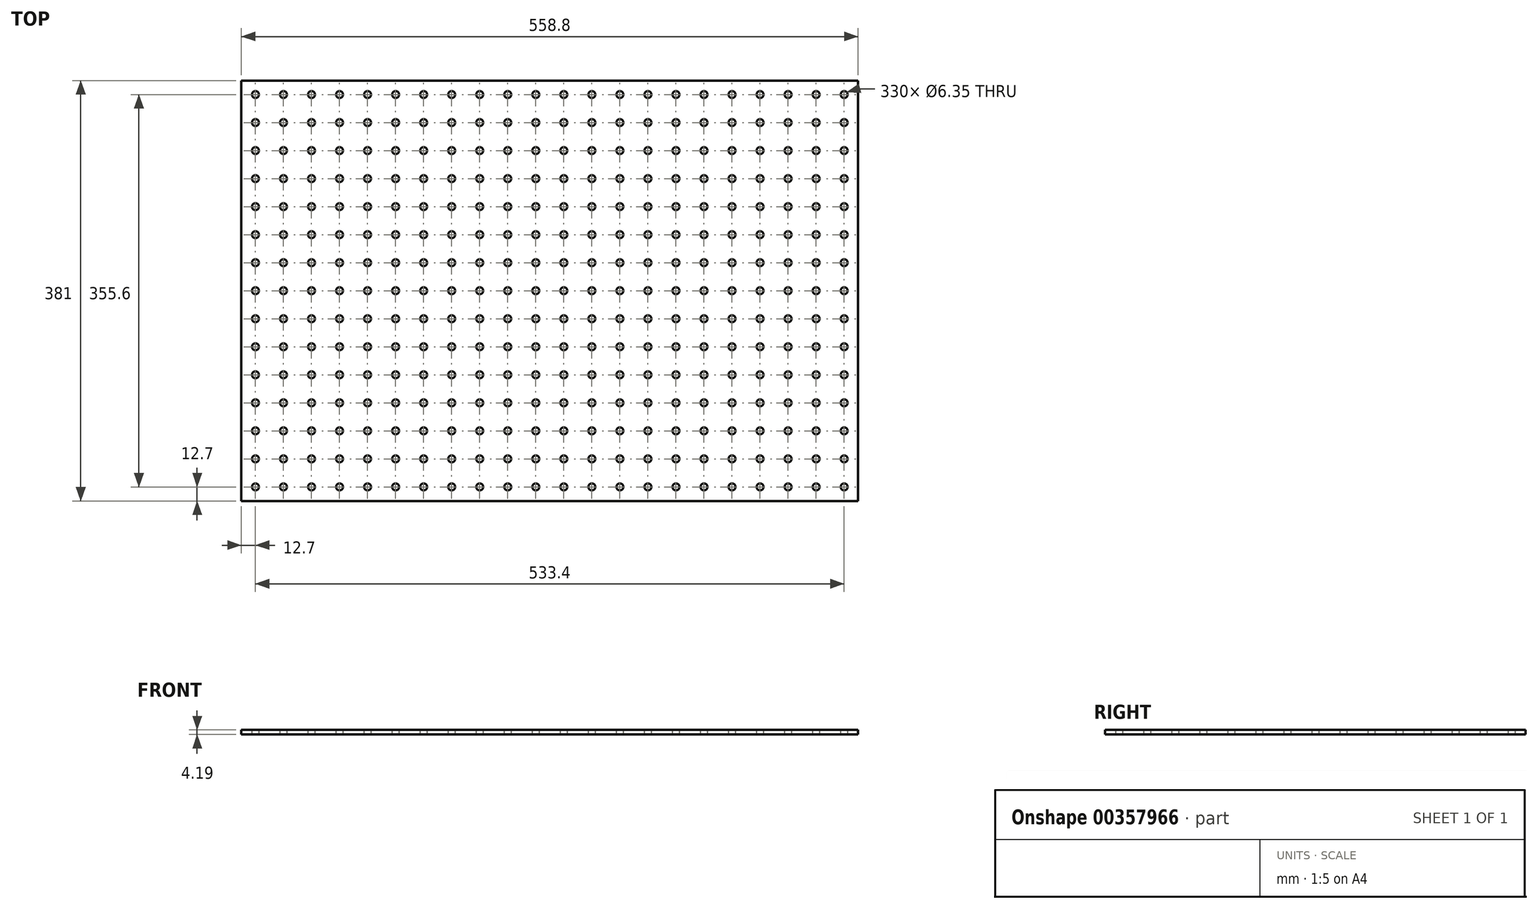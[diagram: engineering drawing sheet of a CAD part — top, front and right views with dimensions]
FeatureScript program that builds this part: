
annotation { "Feature Type Name" : "Feature", "Feature Type Description" : "" }
export const myFeature = defineFeature(function(context is Context, id is Id, definition is map)
    precondition{}
    {
        {
            var Q0;
            Q0=qCreatedBy(makeId("Top.planeOp"),FACE);
            var sketch = newSketch(context, id + "F0", { "sketchPlane" : qUnion([Q0])});
            skLineSegment(sketch, "E0.bottom", {"start": v(279.4, -190.5) * mm, "end": v(-279.4, -190.5) * mm});
            skLineSegment(sketch, "E0.top", {"start": v(279.4, 190.5) * mm, "end": v(-279.4, 190.5) * mm});
            skLineSegment(sketch, "E0.left", {"start": v(279.4, -190.5) * mm, "end": v(279.4, 190.5) * mm});
            skLineSegment(sketch, "E0.right", {"start": v(-279.4, -190.5) * mm, "end": v(-279.4, 190.5) * mm});
            skPoint(sketch, "E0.middle", {"position": v(0, 0) * mm});
            skCircle(sketch, "E1", {"center": v(266.7, 177.8) * mm, "radius": 3.17 * mm});
            skCircle(sketch, "E2.0.1.0", {"center": v(266.7, 152.4) * mm, "radius": 3.17 * mm});
            skCircle(sketch, "E2.0.2.0", {"center": v(266.7, 127) * mm, "radius": 3.17 * mm});
            skCircle(sketch, "E2.0.3.0", {"center": v(266.7, 101.6) * mm, "radius": 3.17 * mm});
            skCircle(sketch, "E2.0.4.0", {"center": v(266.7, 76.2) * mm, "radius": 3.17 * mm});
            skCircle(sketch, "E2.0.5.0", {"center": v(266.7, 50.8) * mm, "radius": 3.17 * mm});
            skCircle(sketch, "E2.0.6.0", {"center": v(266.7, 25.4) * mm, "radius": 3.17 * mm});
            skCircle(sketch, "E2.0.7.0", {"center": v(266.7, 0) * mm, "radius": 3.17 * mm});
            skCircle(sketch, "E2.0.8.0", {"center": v(266.7, -25.4) * mm, "radius": 3.17 * mm});
            skCircle(sketch, "E2.0.9.0", {"center": v(266.7, -50.8) * mm, "radius": 3.17 * mm});
            skCircle(sketch, "E2.0.10.0", {"center": v(266.7, -76.2) * mm, "radius": 3.17 * mm});
            skCircle(sketch, "E2.0.11.0", {"center": v(266.7, -101.6) * mm, "radius": 3.17 * mm});
            skCircle(sketch, "E2.0.12.0", {"center": v(266.7, -127) * mm, "radius": 3.17 * mm});
            skCircle(sketch, "E2.0.13.0", {"center": v(266.7, -152.4) * mm, "radius": 3.17 * mm});
            skCircle(sketch, "E2.0.14.0", {"center": v(266.7, -177.8) * mm, "radius": 3.17 * mm});
            skCircle(sketch, "E2.1.0.0", {"center": v(241.3, 177.8) * mm, "radius": 3.17 * mm});
            skCircle(sketch, "E2.1.1.0", {"center": v(241.3, 152.4) * mm, "radius": 3.17 * mm});
            skCircle(sketch, "E2.1.2.0", {"center": v(241.3, 127) * mm, "radius": 3.17 * mm});
            skCircle(sketch, "E2.1.3.0", {"center": v(241.3, 101.6) * mm, "radius": 3.17 * mm});
            skCircle(sketch, "E2.1.4.0", {"center": v(241.3, 76.2) * mm, "radius": 3.17 * mm});
            skCircle(sketch, "E2.1.5.0", {"center": v(241.3, 50.8) * mm, "radius": 3.17 * mm});
            skCircle(sketch, "E2.1.6.0", {"center": v(241.3, 25.4) * mm, "radius": 3.17 * mm});
            skCircle(sketch, "E2.1.7.0", {"center": v(241.3, 0) * mm, "radius": 3.17 * mm});
            skCircle(sketch, "E2.1.8.0", {"center": v(241.3, -25.4) * mm, "radius": 3.17 * mm});
            skCircle(sketch, "E2.1.9.0", {"center": v(241.3, -50.8) * mm, "radius": 3.17 * mm});
            skCircle(sketch, "E2.1.10.0", {"center": v(241.3, -76.2) * mm, "radius": 3.17 * mm});
            skCircle(sketch, "E2.1.11.0", {"center": v(241.3, -101.6) * mm, "radius": 3.17 * mm});
            skCircle(sketch, "E2.1.12.0", {"center": v(241.3, -127) * mm, "radius": 3.17 * mm});
            skCircle(sketch, "E2.1.13.0", {"center": v(241.3, -152.4) * mm, "radius": 3.17 * mm});
            skCircle(sketch, "E2.1.14.0", {"center": v(241.3, -177.8) * mm, "radius": 3.17 * mm});
            skCircle(sketch, "E2.2.0.0", {"center": v(215.9, 177.8) * mm, "radius": 3.17 * mm});
            skCircle(sketch, "E2.2.1.0", {"center": v(215.9, 152.4) * mm, "radius": 3.17 * mm});
            skCircle(sketch, "E2.2.2.0", {"center": v(215.9, 127) * mm, "radius": 3.17 * mm});
            skCircle(sketch, "E2.2.3.0", {"center": v(215.9, 101.6) * mm, "radius": 3.17 * mm});
            skCircle(sketch, "E2.2.4.0", {"center": v(215.9, 76.2) * mm, "radius": 3.17 * mm});
            skCircle(sketch, "E2.2.5.0", {"center": v(215.9, 50.8) * mm, "radius": 3.17 * mm});
            skCircle(sketch, "E2.2.6.0", {"center": v(215.9, 25.4) * mm, "radius": 3.17 * mm});
            skCircle(sketch, "E2.2.7.0", {"center": v(215.9, 0) * mm, "radius": 3.17 * mm});
            skCircle(sketch, "E2.2.8.0", {"center": v(215.9, -25.4) * mm, "radius": 3.17 * mm});
            skCircle(sketch, "E2.2.9.0", {"center": v(215.9, -50.8) * mm, "radius": 3.17 * mm});
            skCircle(sketch, "E2.2.10.0", {"center": v(215.9, -76.2) * mm, "radius": 3.17 * mm});
            skCircle(sketch, "E2.2.11.0", {"center": v(215.9, -101.6) * mm, "radius": 3.17 * mm});
            skCircle(sketch, "E2.2.12.0", {"center": v(215.9, -127) * mm, "radius": 3.17 * mm});
            skCircle(sketch, "E2.2.13.0", {"center": v(215.9, -152.4) * mm, "radius": 3.17 * mm});
            skCircle(sketch, "E2.2.14.0", {"center": v(215.9, -177.8) * mm, "radius": 3.17 * mm});
            skCircle(sketch, "E2.3.0.0", {"center": v(190.5, 177.8) * mm, "radius": 3.17 * mm});
            skCircle(sketch, "E2.3.1.0", {"center": v(190.5, 152.4) * mm, "radius": 3.17 * mm});
            skCircle(sketch, "E2.3.2.0", {"center": v(190.5, 127) * mm, "radius": 3.17 * mm});
            skCircle(sketch, "E2.3.3.0", {"center": v(190.5, 101.6) * mm, "radius": 3.17 * mm});
            skCircle(sketch, "E2.3.4.0", {"center": v(190.5, 76.2) * mm, "radius": 3.17 * mm});
            skCircle(sketch, "E2.3.5.0", {"center": v(190.5, 50.8) * mm, "radius": 3.17 * mm});
            skCircle(sketch, "E2.3.6.0", {"center": v(190.5, 25.4) * mm, "radius": 3.17 * mm});
            skCircle(sketch, "E2.3.7.0", {"center": v(190.5, 0) * mm, "radius": 3.17 * mm});
            skCircle(sketch, "E2.3.8.0", {"center": v(190.5, -25.4) * mm, "radius": 3.17 * mm});
            skCircle(sketch, "E2.3.9.0", {"center": v(190.5, -50.8) * mm, "radius": 3.17 * mm});
            skCircle(sketch, "E2.3.10.0", {"center": v(190.5, -76.2) * mm, "radius": 3.17 * mm});
            skCircle(sketch, "E2.3.11.0", {"center": v(190.5, -101.6) * mm, "radius": 3.17 * mm});
            skCircle(sketch, "E2.3.12.0", {"center": v(190.5, -127) * mm, "radius": 3.17 * mm});
            skCircle(sketch, "E2.3.13.0", {"center": v(190.5, -152.4) * mm, "radius": 3.17 * mm});
            skCircle(sketch, "E2.3.14.0", {"center": v(190.5, -177.8) * mm, "radius": 3.17 * mm});
            skCircle(sketch, "E2.4.0.0", {"center": v(165.1, 177.8) * mm, "radius": 3.17 * mm});
            skCircle(sketch, "E2.4.1.0", {"center": v(165.1, 152.4) * mm, "radius": 3.17 * mm});
            skCircle(sketch, "E2.4.2.0", {"center": v(165.1, 127) * mm, "radius": 3.17 * mm});
            skCircle(sketch, "E2.4.3.0", {"center": v(165.1, 101.6) * mm, "radius": 3.17 * mm});
            skCircle(sketch, "E2.4.4.0", {"center": v(165.1, 76.2) * mm, "radius": 3.17 * mm});
            skCircle(sketch, "E2.4.5.0", {"center": v(165.1, 50.8) * mm, "radius": 3.17 * mm});
            skCircle(sketch, "E2.4.6.0", {"center": v(165.1, 25.4) * mm, "radius": 3.17 * mm});
            skCircle(sketch, "E2.4.7.0", {"center": v(165.1, 0) * mm, "radius": 3.17 * mm});
            skCircle(sketch, "E2.4.8.0", {"center": v(165.1, -25.4) * mm, "radius": 3.17 * mm});
            skCircle(sketch, "E2.4.9.0", {"center": v(165.1, -50.8) * mm, "radius": 3.17 * mm});
            skCircle(sketch, "E2.4.10.0", {"center": v(165.1, -76.2) * mm, "radius": 3.17 * mm});
            skCircle(sketch, "E2.4.11.0", {"center": v(165.1, -101.6) * mm, "radius": 3.17 * mm});
            skCircle(sketch, "E2.4.12.0", {"center": v(165.1, -127) * mm, "radius": 3.17 * mm});
            skCircle(sketch, "E2.4.13.0", {"center": v(165.1, -152.4) * mm, "radius": 3.17 * mm});
            skCircle(sketch, "E2.4.14.0", {"center": v(165.1, -177.8) * mm, "radius": 3.17 * mm});
            skCircle(sketch, "E2.5.0.0", {"center": v(139.7, 177.8) * mm, "radius": 3.17 * mm});
            skCircle(sketch, "E2.5.1.0", {"center": v(139.7, 152.4) * mm, "radius": 3.17 * mm});
            skCircle(sketch, "E2.5.2.0", {"center": v(139.7, 127) * mm, "radius": 3.17 * mm});
            skCircle(sketch, "E2.5.3.0", {"center": v(139.7, 101.6) * mm, "radius": 3.17 * mm});
            skCircle(sketch, "E2.5.4.0", {"center": v(139.7, 76.2) * mm, "radius": 3.17 * mm});
            skCircle(sketch, "E2.5.5.0", {"center": v(139.7, 50.8) * mm, "radius": 3.17 * mm});
            skCircle(sketch, "E2.5.6.0", {"center": v(139.7, 25.4) * mm, "radius": 3.17 * mm});
            skCircle(sketch, "E2.5.7.0", {"center": v(139.7, 0) * mm, "radius": 3.17 * mm});
            skCircle(sketch, "E2.5.8.0", {"center": v(139.7, -25.4) * mm, "radius": 3.17 * mm});
            skCircle(sketch, "E2.5.9.0", {"center": v(139.7, -50.8) * mm, "radius": 3.17 * mm});
            skCircle(sketch, "E2.5.10.0", {"center": v(139.7, -76.2) * mm, "radius": 3.17 * mm});
            skCircle(sketch, "E2.5.11.0", {"center": v(139.7, -101.6) * mm, "radius": 3.17 * mm});
            skCircle(sketch, "E2.5.12.0", {"center": v(139.7, -127) * mm, "radius": 3.17 * mm});
            skCircle(sketch, "E2.5.13.0", {"center": v(139.7, -152.4) * mm, "radius": 3.17 * mm});
            skCircle(sketch, "E2.5.14.0", {"center": v(139.7, -177.8) * mm, "radius": 3.17 * mm});
            skCircle(sketch, "E2.6.0.0", {"center": v(114.3, 177.8) * mm, "radius": 3.17 * mm});
            skCircle(sketch, "E2.6.1.0", {"center": v(114.3, 152.4) * mm, "radius": 3.17 * mm});
            skCircle(sketch, "E2.6.2.0", {"center": v(114.3, 127) * mm, "radius": 3.17 * mm});
            skCircle(sketch, "E2.6.3.0", {"center": v(114.3, 101.6) * mm, "radius": 3.17 * mm});
            skCircle(sketch, "E2.6.4.0", {"center": v(114.3, 76.2) * mm, "radius": 3.17 * mm});
            skCircle(sketch, "E2.6.5.0", {"center": v(114.3, 50.8) * mm, "radius": 3.17 * mm});
            skCircle(sketch, "E2.6.6.0", {"center": v(114.3, 25.4) * mm, "radius": 3.17 * mm});
            skCircle(sketch, "E2.6.7.0", {"center": v(114.3, 0) * mm, "radius": 3.17 * mm});
            skCircle(sketch, "E2.6.8.0", {"center": v(114.3, -25.4) * mm, "radius": 3.17 * mm});
            skCircle(sketch, "E2.6.9.0", {"center": v(114.3, -50.8) * mm, "radius": 3.17 * mm});
            skCircle(sketch, "E2.6.10.0", {"center": v(114.3, -76.2) * mm, "radius": 3.17 * mm});
            skCircle(sketch, "E2.6.11.0", {"center": v(114.3, -101.6) * mm, "radius": 3.17 * mm});
            skCircle(sketch, "E2.6.12.0", {"center": v(114.3, -127) * mm, "radius": 3.17 * mm});
            skCircle(sketch, "E2.6.13.0", {"center": v(114.3, -152.4) * mm, "radius": 3.17 * mm});
            skCircle(sketch, "E2.6.14.0", {"center": v(114.3, -177.8) * mm, "radius": 3.17 * mm});
            skCircle(sketch, "E2.7.0.0", {"center": v(88.9, 177.8) * mm, "radius": 3.17 * mm});
            skCircle(sketch, "E2.7.1.0", {"center": v(88.9, 152.4) * mm, "radius": 3.17 * mm});
            skCircle(sketch, "E2.7.2.0", {"center": v(88.9, 127) * mm, "radius": 3.17 * mm});
            skCircle(sketch, "E2.7.3.0", {"center": v(88.9, 101.6) * mm, "radius": 3.17 * mm});
            skCircle(sketch, "E2.7.4.0", {"center": v(88.9, 76.2) * mm, "radius": 3.17 * mm});
            skCircle(sketch, "E2.7.5.0", {"center": v(88.9, 50.8) * mm, "radius": 3.17 * mm});
            skCircle(sketch, "E2.7.6.0", {"center": v(88.9, 25.4) * mm, "radius": 3.17 * mm});
            skCircle(sketch, "E2.7.7.0", {"center": v(88.9, 0) * mm, "radius": 3.17 * mm});
            skCircle(sketch, "E2.7.8.0", {"center": v(88.9, -25.4) * mm, "radius": 3.17 * mm});
            skCircle(sketch, "E2.7.9.0", {"center": v(88.9, -50.8) * mm, "radius": 3.17 * mm});
            skCircle(sketch, "E2.7.10.0", {"center": v(88.9, -76.2) * mm, "radius": 3.17 * mm});
            skCircle(sketch, "E2.7.11.0", {"center": v(88.9, -101.6) * mm, "radius": 3.17 * mm});
            skCircle(sketch, "E2.7.12.0", {"center": v(88.9, -127) * mm, "radius": 3.17 * mm});
            skCircle(sketch, "E2.7.13.0", {"center": v(88.9, -152.4) * mm, "radius": 3.17 * mm});
            skCircle(sketch, "E2.7.14.0", {"center": v(88.9, -177.8) * mm, "radius": 3.17 * mm});
            skCircle(sketch, "E2.8.0.0", {"center": v(63.5, 177.8) * mm, "radius": 3.17 * mm});
            skCircle(sketch, "E2.8.1.0", {"center": v(63.5, 152.4) * mm, "radius": 3.17 * mm});
            skCircle(sketch, "E2.8.2.0", {"center": v(63.5, 127) * mm, "radius": 3.17 * mm});
            skCircle(sketch, "E2.8.3.0", {"center": v(63.5, 101.6) * mm, "radius": 3.17 * mm});
            skCircle(sketch, "E2.8.4.0", {"center": v(63.5, 76.2) * mm, "radius": 3.17 * mm});
            skCircle(sketch, "E2.8.5.0", {"center": v(63.5, 50.8) * mm, "radius": 3.17 * mm});
            skCircle(sketch, "E2.8.6.0", {"center": v(63.5, 25.4) * mm, "radius": 3.17 * mm});
            skCircle(sketch, "E2.8.7.0", {"center": v(63.5, 0) * mm, "radius": 3.17 * mm});
            skCircle(sketch, "E2.8.8.0", {"center": v(63.5, -25.4) * mm, "radius": 3.17 * mm});
            skCircle(sketch, "E2.8.9.0", {"center": v(63.5, -50.8) * mm, "radius": 3.17 * mm});
            skCircle(sketch, "E2.8.10.0", {"center": v(63.5, -76.2) * mm, "radius": 3.17 * mm});
            skCircle(sketch, "E2.8.11.0", {"center": v(63.5, -101.6) * mm, "radius": 3.17 * mm});
            skCircle(sketch, "E2.8.12.0", {"center": v(63.5, -127) * mm, "radius": 3.17 * mm});
            skCircle(sketch, "E2.8.13.0", {"center": v(63.5, -152.4) * mm, "radius": 3.17 * mm});
            skCircle(sketch, "E2.8.14.0", {"center": v(63.5, -177.8) * mm, "radius": 3.17 * mm});
            skCircle(sketch, "E2.9.0.0", {"center": v(38.1, 177.8) * mm, "radius": 3.17 * mm});
            skCircle(sketch, "E2.9.1.0", {"center": v(38.1, 152.4) * mm, "radius": 3.17 * mm});
            skCircle(sketch, "E2.9.2.0", {"center": v(38.1, 127) * mm, "radius": 3.17 * mm});
            skCircle(sketch, "E2.9.3.0", {"center": v(38.1, 101.6) * mm, "radius": 3.17 * mm});
            skCircle(sketch, "E2.9.4.0", {"center": v(38.1, 76.2) * mm, "radius": 3.17 * mm});
            skCircle(sketch, "E2.9.5.0", {"center": v(38.1, 50.8) * mm, "radius": 3.17 * mm});
            skCircle(sketch, "E2.9.6.0", {"center": v(38.1, 25.4) * mm, "radius": 3.17 * mm});
            skCircle(sketch, "E2.9.7.0", {"center": v(38.1, 0) * mm, "radius": 3.17 * mm});
            skCircle(sketch, "E2.9.8.0", {"center": v(38.1, -25.4) * mm, "radius": 3.17 * mm});
            skCircle(sketch, "E2.9.9.0", {"center": v(38.1, -50.8) * mm, "radius": 3.17 * mm});
            skCircle(sketch, "E2.9.10.0", {"center": v(38.1, -76.2) * mm, "radius": 3.17 * mm});
            skCircle(sketch, "E2.9.11.0", {"center": v(38.1, -101.6) * mm, "radius": 3.17 * mm});
            skCircle(sketch, "E2.9.12.0", {"center": v(38.1, -127) * mm, "radius": 3.17 * mm});
            skCircle(sketch, "E2.9.13.0", {"center": v(38.1, -152.4) * mm, "radius": 3.17 * mm});
            skCircle(sketch, "E2.9.14.0", {"center": v(38.1, -177.8) * mm, "radius": 3.17 * mm});
            skCircle(sketch, "E2.10.0.0", {"center": v(12.7, 177.8) * mm, "radius": 3.17 * mm});
            skCircle(sketch, "E2.10.1.0", {"center": v(12.7, 152.4) * mm, "radius": 3.17 * mm});
            skCircle(sketch, "E2.10.2.0", {"center": v(12.7, 127) * mm, "radius": 3.17 * mm});
            skCircle(sketch, "E2.10.3.0", {"center": v(12.7, 101.6) * mm, "radius": 3.17 * mm});
            skCircle(sketch, "E2.10.4.0", {"center": v(12.7, 76.2) * mm, "radius": 3.17 * mm});
            skCircle(sketch, "E2.10.5.0", {"center": v(12.7, 50.8) * mm, "radius": 3.17 * mm});
            skCircle(sketch, "E2.10.6.0", {"center": v(12.7, 25.4) * mm, "radius": 3.17 * mm});
            skCircle(sketch, "E2.10.7.0", {"center": v(12.7, 0) * mm, "radius": 3.17 * mm});
            skCircle(sketch, "E2.10.8.0", {"center": v(12.7, -25.4) * mm, "radius": 3.17 * mm});
            skCircle(sketch, "E2.10.9.0", {"center": v(12.7, -50.8) * mm, "radius": 3.17 * mm});
            skCircle(sketch, "E2.10.10.0", {"center": v(12.7, -76.2) * mm, "radius": 3.17 * mm});
            skCircle(sketch, "E2.10.11.0", {"center": v(12.7, -101.6) * mm, "radius": 3.17 * mm});
            skCircle(sketch, "E2.10.12.0", {"center": v(12.7, -127) * mm, "radius": 3.17 * mm});
            skCircle(sketch, "E2.10.13.0", {"center": v(12.7, -152.4) * mm, "radius": 3.17 * mm});
            skCircle(sketch, "E2.10.14.0", {"center": v(12.7, -177.8) * mm, "radius": 3.17 * mm});
            skCircle(sketch, "E2.11.0.0", {"center": v(-12.7, 177.8) * mm, "radius": 3.17 * mm});
            skCircle(sketch, "E2.11.1.0", {"center": v(-12.7, 152.4) * mm, "radius": 3.17 * mm});
            skCircle(sketch, "E2.11.2.0", {"center": v(-12.7, 127) * mm, "radius": 3.17 * mm});
            skCircle(sketch, "E2.11.3.0", {"center": v(-12.7, 101.6) * mm, "radius": 3.17 * mm});
            skCircle(sketch, "E2.11.4.0", {"center": v(-12.7, 76.2) * mm, "radius": 3.17 * mm});
            skCircle(sketch, "E2.11.5.0", {"center": v(-12.7, 50.8) * mm, "radius": 3.17 * mm});
            skCircle(sketch, "E2.11.6.0", {"center": v(-12.7, 25.4) * mm, "radius": 3.17 * mm});
            skCircle(sketch, "E2.11.7.0", {"center": v(-12.7, 0) * mm, "radius": 3.17 * mm});
            skCircle(sketch, "E2.11.8.0", {"center": v(-12.7, -25.4) * mm, "radius": 3.17 * mm});
            skCircle(sketch, "E2.11.9.0", {"center": v(-12.7, -50.8) * mm, "radius": 3.17 * mm});
            skCircle(sketch, "E2.11.10.0", {"center": v(-12.7, -76.2) * mm, "radius": 3.17 * mm});
            skCircle(sketch, "E2.11.11.0", {"center": v(-12.7, -101.6) * mm, "radius": 3.17 * mm});
            skCircle(sketch, "E2.11.12.0", {"center": v(-12.7, -127) * mm, "radius": 3.17 * mm});
            skCircle(sketch, "E2.11.13.0", {"center": v(-12.7, -152.4) * mm, "radius": 3.17 * mm});
            skCircle(sketch, "E2.11.14.0", {"center": v(-12.7, -177.8) * mm, "radius": 3.17 * mm});
            skCircle(sketch, "E2.12.0.0", {"center": v(-38.1, 177.8) * mm, "radius": 3.17 * mm});
            skCircle(sketch, "E2.12.1.0", {"center": v(-38.1, 152.4) * mm, "radius": 3.17 * mm});
            skCircle(sketch, "E2.12.2.0", {"center": v(-38.1, 127) * mm, "radius": 3.17 * mm});
            skCircle(sketch, "E2.12.3.0", {"center": v(-38.1, 101.6) * mm, "radius": 3.17 * mm});
            skCircle(sketch, "E2.12.4.0", {"center": v(-38.1, 76.2) * mm, "radius": 3.17 * mm});
            skCircle(sketch, "E2.12.5.0", {"center": v(-38.1, 50.8) * mm, "radius": 3.17 * mm});
            skCircle(sketch, "E2.12.6.0", {"center": v(-38.1, 25.4) * mm, "radius": 3.17 * mm});
            skCircle(sketch, "E2.12.7.0", {"center": v(-38.1, 0) * mm, "radius": 3.17 * mm});
            skCircle(sketch, "E2.12.8.0", {"center": v(-38.1, -25.4) * mm, "radius": 3.17 * mm});
            skCircle(sketch, "E2.12.9.0", {"center": v(-38.1, -50.8) * mm, "radius": 3.17 * mm});
            skCircle(sketch, "E2.12.10.0", {"center": v(-38.1, -76.2) * mm, "radius": 3.17 * mm});
            skCircle(sketch, "E2.12.11.0", {"center": v(-38.1, -101.6) * mm, "radius": 3.17 * mm});
            skCircle(sketch, "E2.12.12.0", {"center": v(-38.1, -127) * mm, "radius": 3.17 * mm});
            skCircle(sketch, "E2.12.13.0", {"center": v(-38.1, -152.4) * mm, "radius": 3.17 * mm});
            skCircle(sketch, "E2.12.14.0", {"center": v(-38.1, -177.8) * mm, "radius": 3.17 * mm});
            skCircle(sketch, "E2.13.0.0", {"center": v(-63.5, 177.8) * mm, "radius": 3.17 * mm});
            skCircle(sketch, "E2.13.1.0", {"center": v(-63.5, 152.4) * mm, "radius": 3.17 * mm});
            skCircle(sketch, "E2.13.2.0", {"center": v(-63.5, 127) * mm, "radius": 3.17 * mm});
            skCircle(sketch, "E2.13.3.0", {"center": v(-63.5, 101.6) * mm, "radius": 3.17 * mm});
            skCircle(sketch, "E2.13.4.0", {"center": v(-63.5, 76.2) * mm, "radius": 3.17 * mm});
            skCircle(sketch, "E2.13.5.0", {"center": v(-63.5, 50.8) * mm, "radius": 3.17 * mm});
            skCircle(sketch, "E2.13.6.0", {"center": v(-63.5, 25.4) * mm, "radius": 3.17 * mm});
            skCircle(sketch, "E2.13.7.0", {"center": v(-63.5, 0) * mm, "radius": 3.17 * mm});
            skCircle(sketch, "E2.13.8.0", {"center": v(-63.5, -25.4) * mm, "radius": 3.17 * mm});
            skCircle(sketch, "E2.13.9.0", {"center": v(-63.5, -50.8) * mm, "radius": 3.17 * mm});
            skCircle(sketch, "E2.13.10.0", {"center": v(-63.5, -76.2) * mm, "radius": 3.17 * mm});
            skCircle(sketch, "E2.13.11.0", {"center": v(-63.5, -101.6) * mm, "radius": 3.17 * mm});
            skCircle(sketch, "E2.13.12.0", {"center": v(-63.5, -127) * mm, "radius": 3.17 * mm});
            skCircle(sketch, "E2.13.13.0", {"center": v(-63.5, -152.4) * mm, "radius": 3.17 * mm});
            skCircle(sketch, "E2.13.14.0", {"center": v(-63.5, -177.8) * mm, "radius": 3.17 * mm});
            skCircle(sketch, "E2.14.0.0", {"center": v(-88.9, 177.8) * mm, "radius": 3.17 * mm});
            skCircle(sketch, "E2.14.1.0", {"center": v(-88.9, 152.4) * mm, "radius": 3.17 * mm});
            skCircle(sketch, "E2.14.2.0", {"center": v(-88.9, 127) * mm, "radius": 3.17 * mm});
            skCircle(sketch, "E2.14.3.0", {"center": v(-88.9, 101.6) * mm, "radius": 3.17 * mm});
            skCircle(sketch, "E2.14.4.0", {"center": v(-88.9, 76.2) * mm, "radius": 3.17 * mm});
            skCircle(sketch, "E2.14.5.0", {"center": v(-88.9, 50.8) * mm, "radius": 3.17 * mm});
            skCircle(sketch, "E2.14.6.0", {"center": v(-88.9, 25.4) * mm, "radius": 3.17 * mm});
            skCircle(sketch, "E2.14.7.0", {"center": v(-88.9, 0) * mm, "radius": 3.17 * mm});
            skCircle(sketch, "E2.14.8.0", {"center": v(-88.9, -25.4) * mm, "radius": 3.17 * mm});
            skCircle(sketch, "E2.14.9.0", {"center": v(-88.9, -50.8) * mm, "radius": 3.17 * mm});
            skCircle(sketch, "E2.14.10.0", {"center": v(-88.9, -76.2) * mm, "radius": 3.17 * mm});
            skCircle(sketch, "E2.14.11.0", {"center": v(-88.9, -101.6) * mm, "radius": 3.17 * mm});
            skCircle(sketch, "E2.14.12.0", {"center": v(-88.9, -127) * mm, "radius": 3.17 * mm});
            skCircle(sketch, "E2.14.13.0", {"center": v(-88.9, -152.4) * mm, "radius": 3.17 * mm});
            skCircle(sketch, "E2.14.14.0", {"center": v(-88.9, -177.8) * mm, "radius": 3.17 * mm});
            skCircle(sketch, "E2.15.0.0", {"center": v(-114.3, 177.8) * mm, "radius": 3.17 * mm});
            skCircle(sketch, "E2.15.1.0", {"center": v(-114.3, 152.4) * mm, "radius": 3.17 * mm});
            skCircle(sketch, "E2.15.2.0", {"center": v(-114.3, 127) * mm, "radius": 3.17 * mm});
            skCircle(sketch, "E2.15.3.0", {"center": v(-114.3, 101.6) * mm, "radius": 3.17 * mm});
            skCircle(sketch, "E2.15.4.0", {"center": v(-114.3, 76.2) * mm, "radius": 3.17 * mm});
            skCircle(sketch, "E2.15.5.0", {"center": v(-114.3, 50.8) * mm, "radius": 3.17 * mm});
            skCircle(sketch, "E2.15.6.0", {"center": v(-114.3, 25.4) * mm, "radius": 3.17 * mm});
            skCircle(sketch, "E2.15.7.0", {"center": v(-114.3, 0) * mm, "radius": 3.17 * mm});
            skCircle(sketch, "E2.15.8.0", {"center": v(-114.3, -25.4) * mm, "radius": 3.17 * mm});
            skCircle(sketch, "E2.15.9.0", {"center": v(-114.3, -50.8) * mm, "radius": 3.17 * mm});
            skCircle(sketch, "E2.15.10.0", {"center": v(-114.3, -76.2) * mm, "radius": 3.17 * mm});
            skCircle(sketch, "E2.15.11.0", {"center": v(-114.3, -101.6) * mm, "radius": 3.17 * mm});
            skCircle(sketch, "E2.15.12.0", {"center": v(-114.3, -127) * mm, "radius": 3.17 * mm});
            skCircle(sketch, "E2.15.13.0", {"center": v(-114.3, -152.4) * mm, "radius": 3.17 * mm});
            skCircle(sketch, "E2.15.14.0", {"center": v(-114.3, -177.8) * mm, "radius": 3.17 * mm});
            skCircle(sketch, "E2.16.0.0", {"center": v(-139.7, 177.8) * mm, "radius": 3.17 * mm});
            skCircle(sketch, "E2.16.1.0", {"center": v(-139.7, 152.4) * mm, "radius": 3.17 * mm});
            skCircle(sketch, "E2.16.2.0", {"center": v(-139.7, 127) * mm, "radius": 3.17 * mm});
            skCircle(sketch, "E2.16.3.0", {"center": v(-139.7, 101.6) * mm, "radius": 3.17 * mm});
            skCircle(sketch, "E2.16.4.0", {"center": v(-139.7, 76.2) * mm, "radius": 3.17 * mm});
            skCircle(sketch, "E2.16.5.0", {"center": v(-139.7, 50.8) * mm, "radius": 3.17 * mm});
            skCircle(sketch, "E2.16.6.0", {"center": v(-139.7, 25.4) * mm, "radius": 3.17 * mm});
            skCircle(sketch, "E2.16.7.0", {"center": v(-139.7, 0) * mm, "radius": 3.17 * mm});
            skCircle(sketch, "E2.16.8.0", {"center": v(-139.7, -25.4) * mm, "radius": 3.17 * mm});
            skCircle(sketch, "E2.16.9.0", {"center": v(-139.7, -50.8) * mm, "radius": 3.17 * mm});
            skCircle(sketch, "E2.16.10.0", {"center": v(-139.7, -76.2) * mm, "radius": 3.17 * mm});
            skCircle(sketch, "E2.16.11.0", {"center": v(-139.7, -101.6) * mm, "radius": 3.17 * mm});
            skCircle(sketch, "E2.16.12.0", {"center": v(-139.7, -127) * mm, "radius": 3.17 * mm});
            skCircle(sketch, "E2.16.13.0", {"center": v(-139.7, -152.4) * mm, "radius": 3.17 * mm});
            skCircle(sketch, "E2.16.14.0", {"center": v(-139.7, -177.8) * mm, "radius": 3.17 * mm});
            skCircle(sketch, "E2.17.0.0", {"center": v(-165.1, 177.8) * mm, "radius": 3.17 * mm});
            skCircle(sketch, "E2.17.1.0", {"center": v(-165.1, 152.4) * mm, "radius": 3.17 * mm});
            skCircle(sketch, "E2.17.2.0", {"center": v(-165.1, 127) * mm, "radius": 3.17 * mm});
            skCircle(sketch, "E2.17.3.0", {"center": v(-165.1, 101.6) * mm, "radius": 3.17 * mm});
            skCircle(sketch, "E2.17.4.0", {"center": v(-165.1, 76.2) * mm, "radius": 3.17 * mm});
            skCircle(sketch, "E2.17.5.0", {"center": v(-165.1, 50.8) * mm, "radius": 3.17 * mm});
            skCircle(sketch, "E2.17.6.0", {"center": v(-165.1, 25.4) * mm, "radius": 3.17 * mm});
            skCircle(sketch, "E2.17.7.0", {"center": v(-165.1, 0) * mm, "radius": 3.17 * mm});
            skCircle(sketch, "E2.17.8.0", {"center": v(-165.1, -25.4) * mm, "radius": 3.17 * mm});
            skCircle(sketch, "E2.17.9.0", {"center": v(-165.1, -50.8) * mm, "radius": 3.17 * mm});
            skCircle(sketch, "E2.17.10.0", {"center": v(-165.1, -76.2) * mm, "radius": 3.17 * mm});
            skCircle(sketch, "E2.17.11.0", {"center": v(-165.1, -101.6) * mm, "radius": 3.17 * mm});
            skCircle(sketch, "E2.17.12.0", {"center": v(-165.1, -127) * mm, "radius": 3.17 * mm});
            skCircle(sketch, "E2.17.13.0", {"center": v(-165.1, -152.4) * mm, "radius": 3.17 * mm});
            skCircle(sketch, "E2.17.14.0", {"center": v(-165.1, -177.8) * mm, "radius": 3.17 * mm});
            skCircle(sketch, "E2.18.0.0", {"center": v(-190.5, 177.8) * mm, "radius": 3.17 * mm});
            skCircle(sketch, "E2.18.1.0", {"center": v(-190.5, 152.4) * mm, "radius": 3.17 * mm});
            skCircle(sketch, "E2.18.2.0", {"center": v(-190.5, 127) * mm, "radius": 3.17 * mm});
            skCircle(sketch, "E2.18.3.0", {"center": v(-190.5, 101.6) * mm, "radius": 3.17 * mm});
            skCircle(sketch, "E2.18.4.0", {"center": v(-190.5, 76.2) * mm, "radius": 3.17 * mm});
            skCircle(sketch, "E2.18.5.0", {"center": v(-190.5, 50.8) * mm, "radius": 3.17 * mm});
            skCircle(sketch, "E2.18.6.0", {"center": v(-190.5, 25.4) * mm, "radius": 3.17 * mm});
            skCircle(sketch, "E2.18.7.0", {"center": v(-190.5, 0) * mm, "radius": 3.17 * mm});
            skCircle(sketch, "E2.18.8.0", {"center": v(-190.5, -25.4) * mm, "radius": 3.17 * mm});
            skCircle(sketch, "E2.18.9.0", {"center": v(-190.5, -50.8) * mm, "radius": 3.17 * mm});
            skCircle(sketch, "E2.18.10.0", {"center": v(-190.5, -76.2) * mm, "radius": 3.17 * mm});
            skCircle(sketch, "E2.18.11.0", {"center": v(-190.5, -101.6) * mm, "radius": 3.17 * mm});
            skCircle(sketch, "E2.18.12.0", {"center": v(-190.5, -127) * mm, "radius": 3.17 * mm});
            skCircle(sketch, "E2.18.13.0", {"center": v(-190.5, -152.4) * mm, "radius": 3.17 * mm});
            skCircle(sketch, "E2.18.14.0", {"center": v(-190.5, -177.8) * mm, "radius": 3.17 * mm});
            skCircle(sketch, "E2.19.0.0", {"center": v(-215.9, 177.8) * mm, "radius": 3.17 * mm});
            skCircle(sketch, "E2.19.1.0", {"center": v(-215.9, 152.4) * mm, "radius": 3.17 * mm});
            skCircle(sketch, "E2.19.2.0", {"center": v(-215.9, 127) * mm, "radius": 3.17 * mm});
            skCircle(sketch, "E2.19.3.0", {"center": v(-215.9, 101.6) * mm, "radius": 3.17 * mm});
            skCircle(sketch, "E2.19.4.0", {"center": v(-215.9, 76.2) * mm, "radius": 3.17 * mm});
            skCircle(sketch, "E2.19.5.0", {"center": v(-215.9, 50.8) * mm, "radius": 3.17 * mm});
            skCircle(sketch, "E2.19.6.0", {"center": v(-215.9, 25.4) * mm, "radius": 3.17 * mm});
            skCircle(sketch, "E2.19.7.0", {"center": v(-215.9, 0) * mm, "radius": 3.17 * mm});
            skCircle(sketch, "E2.19.8.0", {"center": v(-215.9, -25.4) * mm, "radius": 3.17 * mm});
            skCircle(sketch, "E2.19.9.0", {"center": v(-215.9, -50.8) * mm, "radius": 3.17 * mm});
            skCircle(sketch, "E2.19.10.0", {"center": v(-215.9, -76.2) * mm, "radius": 3.17 * mm});
            skCircle(sketch, "E2.19.11.0", {"center": v(-215.9, -101.6) * mm, "radius": 3.17 * mm});
            skCircle(sketch, "E2.19.12.0", {"center": v(-215.9, -127) * mm, "radius": 3.17 * mm});
            skCircle(sketch, "E2.19.13.0", {"center": v(-215.9, -152.4) * mm, "radius": 3.17 * mm});
            skCircle(sketch, "E2.19.14.0", {"center": v(-215.9, -177.8) * mm, "radius": 3.17 * mm});
            skCircle(sketch, "E2.20.0.0", {"center": v(-241.3, 177.8) * mm, "radius": 3.17 * mm});
            skCircle(sketch, "E2.20.1.0", {"center": v(-241.3, 152.4) * mm, "radius": 3.17 * mm});
            skCircle(sketch, "E2.20.2.0", {"center": v(-241.3, 127) * mm, "radius": 3.17 * mm});
            skCircle(sketch, "E2.20.3.0", {"center": v(-241.3, 101.6) * mm, "radius": 3.17 * mm});
            skCircle(sketch, "E2.20.4.0", {"center": v(-241.3, 76.2) * mm, "radius": 3.17 * mm});
            skCircle(sketch, "E2.20.5.0", {"center": v(-241.3, 50.8) * mm, "radius": 3.17 * mm});
            skCircle(sketch, "E2.20.6.0", {"center": v(-241.3, 25.4) * mm, "radius": 3.17 * mm});
            skCircle(sketch, "E2.20.7.0", {"center": v(-241.3, 0) * mm, "radius": 3.17 * mm});
            skCircle(sketch, "E2.20.8.0", {"center": v(-241.3, -25.4) * mm, "radius": 3.17 * mm});
            skCircle(sketch, "E2.20.9.0", {"center": v(-241.3, -50.8) * mm, "radius": 3.17 * mm});
            skCircle(sketch, "E2.20.10.0", {"center": v(-241.3, -76.2) * mm, "radius": 3.17 * mm});
            skCircle(sketch, "E2.20.11.0", {"center": v(-241.3, -101.6) * mm, "radius": 3.17 * mm});
            skCircle(sketch, "E2.20.12.0", {"center": v(-241.3, -127) * mm, "radius": 3.17 * mm});
            skCircle(sketch, "E2.20.13.0", {"center": v(-241.3, -152.4) * mm, "radius": 3.17 * mm});
            skCircle(sketch, "E2.20.14.0", {"center": v(-241.3, -177.8) * mm, "radius": 3.17 * mm});
            skCircle(sketch, "E2.21.0.0", {"center": v(-266.7, 177.8) * mm, "radius": 3.17 * mm});
            skCircle(sketch, "E2.21.1.0", {"center": v(-266.7, 152.4) * mm, "radius": 3.17 * mm});
            skCircle(sketch, "E2.21.2.0", {"center": v(-266.7, 127) * mm, "radius": 3.17 * mm});
            skCircle(sketch, "E2.21.3.0", {"center": v(-266.7, 101.6) * mm, "radius": 3.17 * mm});
            skCircle(sketch, "E2.21.4.0", {"center": v(-266.7, 76.2) * mm, "radius": 3.17 * mm});
            skCircle(sketch, "E2.21.5.0", {"center": v(-266.7, 50.8) * mm, "radius": 3.17 * mm});
            skCircle(sketch, "E2.21.6.0", {"center": v(-266.7, 25.4) * mm, "radius": 3.17 * mm});
            skCircle(sketch, "E2.21.7.0", {"center": v(-266.7, 0) * mm, "radius": 3.17 * mm});
            skCircle(sketch, "E2.21.8.0", {"center": v(-266.7, -25.4) * mm, "radius": 3.17 * mm});
            skCircle(sketch, "E2.21.9.0", {"center": v(-266.7, -50.8) * mm, "radius": 3.17 * mm});
            skCircle(sketch, "E2.21.10.0", {"center": v(-266.7, -76.2) * mm, "radius": 3.17 * mm});
            skCircle(sketch, "E2.21.11.0", {"center": v(-266.7, -101.6) * mm, "radius": 3.17 * mm});
            skCircle(sketch, "E2.21.12.0", {"center": v(-266.7, -127) * mm, "radius": 3.17 * mm});
            skCircle(sketch, "E2.21.13.0", {"center": v(-266.7, -152.4) * mm, "radius": 3.17 * mm});
            skCircle(sketch, "E2.21.14.0", {"center": v(-266.7, -177.8) * mm, "radius": 3.17 * mm});
            skLineSegment(sketch, "E2.direction1", {"start": v(266.7, 177.8) * mm, "end": v(241.3, 177.8) * mm, "construction": true});
            skLineSegment(sketch, "E2.direction2", {"start": v(266.7, 177.8) * mm, "end": v(266.7, 152.4) * mm, "construction": true});
            skSolve(sketch);
        }
        {
            var Q0;
            Q0=makeQuery(id+"F0.imprint","IMPRINT",FACE,{"disambiguationData":[TD([[makeQuery(id+"F0.imprint","IMPRINT",EDGE,{"derivedFrom":sQuery(id+"F0.wireOp",EDGE,"E0.bottom")}),-1.0]])]});
            extrude(context, id + "F1", {"entities" : qUnion([Q0]), "depth" : 4.2 * mm});
        }
    });
